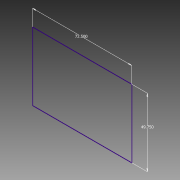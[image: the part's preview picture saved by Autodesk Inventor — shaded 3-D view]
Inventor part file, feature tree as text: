
AUTODESK INVENTOR PART (.ipt)
format: ipt  version: 2013 (Build 170138000, 138)  size: 60,928 bytes
history: native  units: in
note: dims shown in document units (in); Inventor stores cm internally (conversion verified against a paired STEP export)
features: sketch x1
ambient origin geometry x8: Origin, YZ Plane, XZ Plane, XY Plane, X Axis, Y Axis, Z Axis, Center Point
feature tree (1):
  sketch  "Sketch1"  dims[d0=72.5in d1=49.75in]
